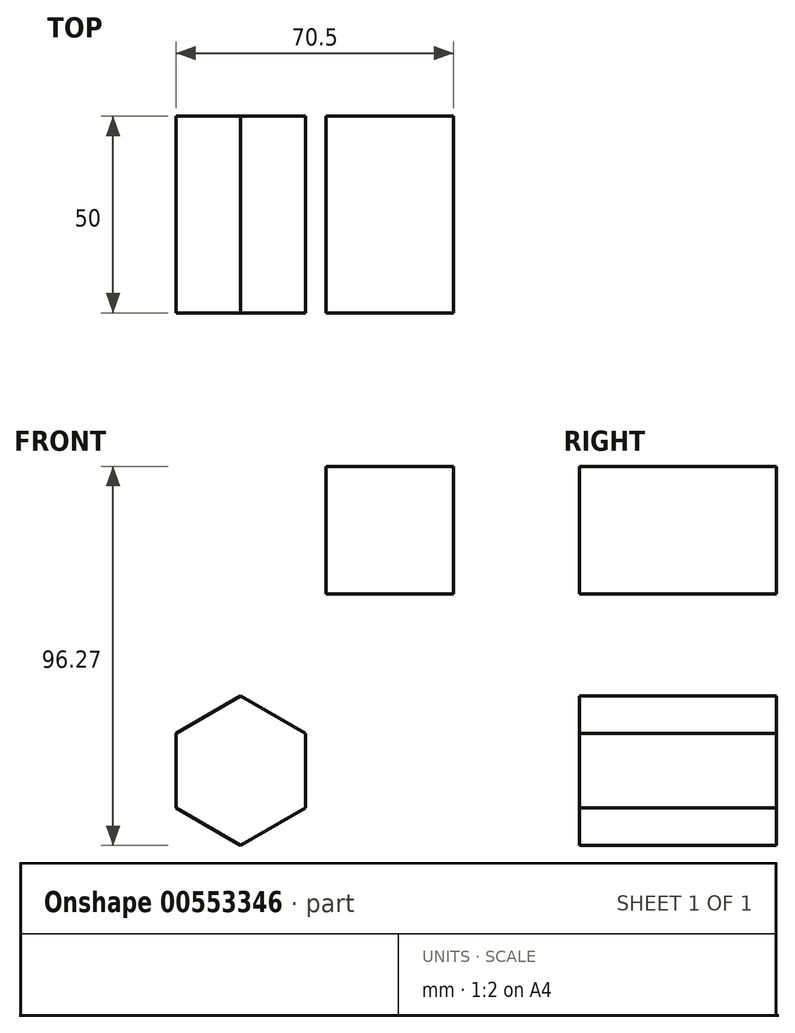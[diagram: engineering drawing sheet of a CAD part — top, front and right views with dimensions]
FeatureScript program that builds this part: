
annotation { "Feature Type Name" : "Feature", "Feature Type Description" : "" }
export const myFeature = defineFeature(function(context is Context, id is Id, definition is map)
    precondition{}
    {
        {
            var Q0;
            Q0=qCreatedBy(makeId("Front.planeOp"),FACE);
            var sketch = newSketch(context, id + "F0", { "sketchPlane" : qUnion([Q0])});
            skLineSegment(sketch, "E0", {"start": v(0, 0) * mm, "end": v(-16.45, -9.5) * mm});
            skLineSegment(sketch, "E1", {"start": v(-16.45, -9.5) * mm, "end": v(-16.45, -28.49) * mm});
            skLineSegment(sketch, "E2", {"start": v(-16.45, -28.49) * mm, "end": v(0, -37.98) * mm});
            skLineSegment(sketch, "E3", {"start": v(0, -37.98) * mm, "end": v(16.45, -28.49) * mm});
            skLineSegment(sketch, "E4", {"start": v(0, 0) * mm, "end": v(16.45, -9.5) * mm});
            skLineSegment(sketch, "E5", {"start": v(16.45, -9.5) * mm, "end": v(16.45, -28.49) * mm});
            skLineSegment(sketch, "E6.bottom", {"start": v(21.62, 58.29) * mm, "end": v(54.05, 58.29) * mm});
            skLineSegment(sketch, "E6.top", {"start": v(21.62, 25.86) * mm, "end": v(54.05, 25.86) * mm});
            skLineSegment(sketch, "E6.left", {"start": v(21.62, 58.29) * mm, "end": v(21.62, 25.86) * mm});
            skLineSegment(sketch, "E6.right", {"start": v(54.05, 58.29) * mm, "end": v(54.05, 25.86) * mm});
            skSolve(sketch);
        }
        {
            var Q0;
            Q0 = qSketchRegion(id + "F0", true);
            extrude(context, id + "F1", {"entities" : qUnion([Q0]), "depth" : 50 * mm, "offsetDistance" : 25 * mm});
        }
    });
